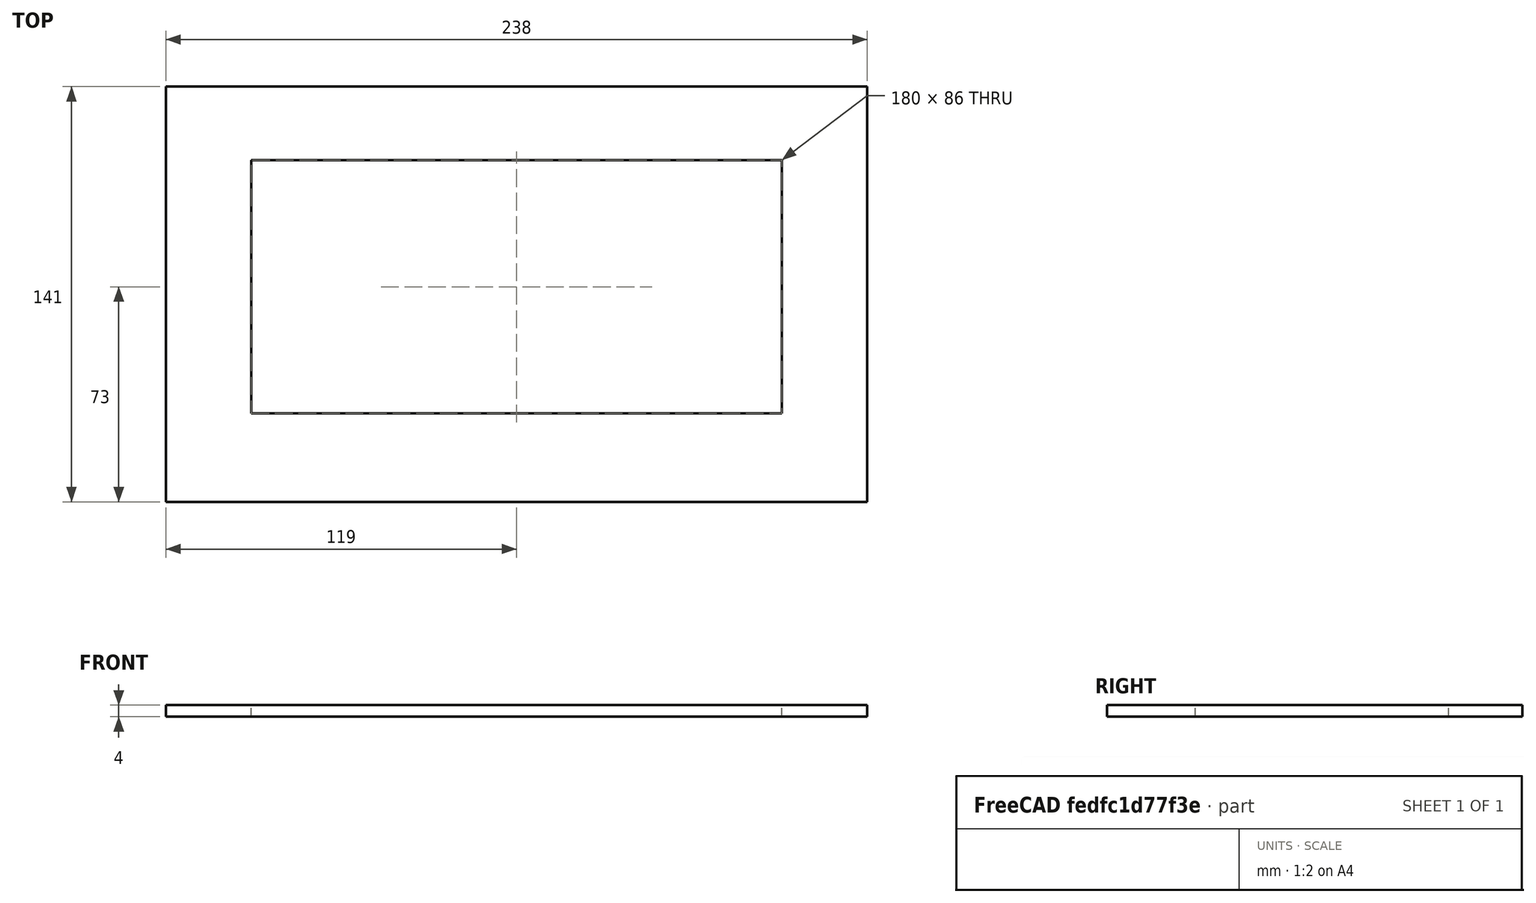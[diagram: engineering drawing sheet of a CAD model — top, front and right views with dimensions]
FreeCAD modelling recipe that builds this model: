
FCSTD DOCUMENT  (FreeCAD 0.19R24366 (Git))
Label: Blende
License: All rights reserved
LicenseURL: http://en.wikipedia.org/wiki/All_rights_reserved
objects: Sketcher::SketchObject×2, PartDesign::Pad×1, PartDesign::Body×1, TechDraw::DrawSVGTemplate×1, TechDraw::DrawViewPart×1, TechDraw::DrawPage×1, Part::Part2DObjectPython×1
note: 6 computed .brp shape members not serialized (recipe doc carries the construction recipe); baked Part::Feature solids carry a one-line shape summary decoded from their .brp

FEATURE [Sketcher::SketchObject] Sketch
  FullyConstrained = true
  MapMode = 5
  Support = -> [XY_Plane]
  sketch-geometry (8):
    g0: LineSegment StartX=-90 StartY=45.5 StartZ=0 EndX=90 EndY=45.5 EndZ=0
    g1: LineSegment StartX=90 StartY=45.5 StartZ=0 EndX=90 EndY=-40.5 EndZ=0
    g2: LineSegment StartX=90 StartY=-40.5 StartZ=0 EndX=-90 EndY=-40.5 EndZ=0
    g3: LineSegment StartX=-90 StartY=-40.5 StartZ=0 EndX=-90 EndY=45.5 EndZ=0
    g4: LineSegment StartX=-119 StartY=70.5 StartZ=0 EndX=119 EndY=70.5 EndZ=0
    g5: LineSegment StartX=119 StartY=70.5 StartZ=0 EndX=119 EndY=-70.5 EndZ=0
    g6: LineSegment StartX=119 StartY=-70.5 StartZ=0 EndX=-119 EndY=-70.5 EndZ=0
    g7: LineSegment StartX=-119 StartY=-70.5 StartZ=0 EndX=-119 EndY=70.5 EndZ=0
  constraints (23):
    c: Coincident(g0,g1)
    c: Coincident(g1,g2)
    c: Coincident(g2,g3)
    c: Coincident(g3,g0)
    c: Horizontal(g0)
    c: Horizontal(g2)
    c: Vertical(g1)
    c: Vertical(g3)
    c: Coincident(g4,g5)
    c: Coincident(g5,g6)
    c: Coincident(g6,g7)
    c: Coincident(g7,g4)
    c: Horizontal(g4)
    c: Horizontal(g6)
    c: Vertical(g5)
    c: Vertical(g7)
    c: DistanceY(g3,g3) = 86
    c: DistanceX(g0,g0) = 180
    c: DistanceX(g4,g4) = 238
    c: DistanceY(g5,g5) = 141
    c: Symmetric(g5,g4,g-1)
    c: DistanceY(g0,g4) = 25
    c: DistanceX(g4,g0) = 29
FEATURE [PartDesign::Pad] Pad
  Direction = (1,1,1)
  Length = 4
  Length2 = 100
  Profile = -> Sketch
  Refine = true
  Type = 0
FEATURE [PartDesign::Body] Body
  Group = -> [Sketch,Pad]
  Origin = -> Origin
  Tip = -> Pad
FEATURE [TechDraw::DrawSVGTemplate] Template
  Height = 841
  Orientation = 1
  Width = 1189
FEATURE [TechDraw::DrawViewPart] View
  CoarseView = false
  Direction = (0,0,1)
  Focus = 100
  HardHidden = false
  IsoCount = 0
  IsoHidden = false
  IsoVisible = false
  LockPosition = false
  Perspective = false
  Rotation = 0
  ScaleType = 0
  SeamHidden = false
  SeamVisible = true
  SmoothHidden = false
  SmoothVisible = true
  Source = -> [Body]
  X = 594.5
  XDirection = (1,0,0)
  Y = 420.5
FEATURE [TechDraw::DrawPage] Page
  KeepUpdated = true
  NextBalloonIndex = 1
  ProjectionType = 0
  Template = -> Template
  Views = -> [View]
FEATURE [Part::Part2DObjectPython] Shape2DView  # Draft 2D object (typed FeaturePython)
  Base = -> Body
  FuseArch = false
  HiddenLines = false
  InPlace = true
  Projection = (0,0,1)
  ProjectionMode = 0
  SegmentLength = 0.05
  Tessellation = false
  VisibleOnly = false
FEATURE [Sketcher::SketchObject] Sketch001
  FullyConstrained = false
  sketch-geometry (8):
    g0: LineSegment StartX=-119 StartY=70.5 StartZ=0 EndX=119 EndY=70.5 EndZ=0
    g1: LineSegment StartX=119 StartY=70.5 StartZ=0 EndX=119 EndY=-70.5 EndZ=0
    g2: LineSegment StartX=119 StartY=-70.5 StartZ=0 EndX=-119 EndY=-70.5 EndZ=0
    g3: LineSegment StartX=-119 StartY=-70.5 StartZ=0 EndX=-119 EndY=70.5 EndZ=0
    g4: LineSegment StartX=-90 StartY=-40.5 StartZ=0 EndX=-90 EndY=45.5 EndZ=0
    g5: LineSegment StartX=90 StartY=-40.5 StartZ=0 EndX=-90 EndY=-40.5 EndZ=0
    g6: LineSegment StartX=90 StartY=45.5 StartZ=0 EndX=90 EndY=-40.5 EndZ=0
    g7: LineSegment StartX=-90 StartY=45.5 StartZ=0 EndX=90 EndY=45.5 EndZ=0
